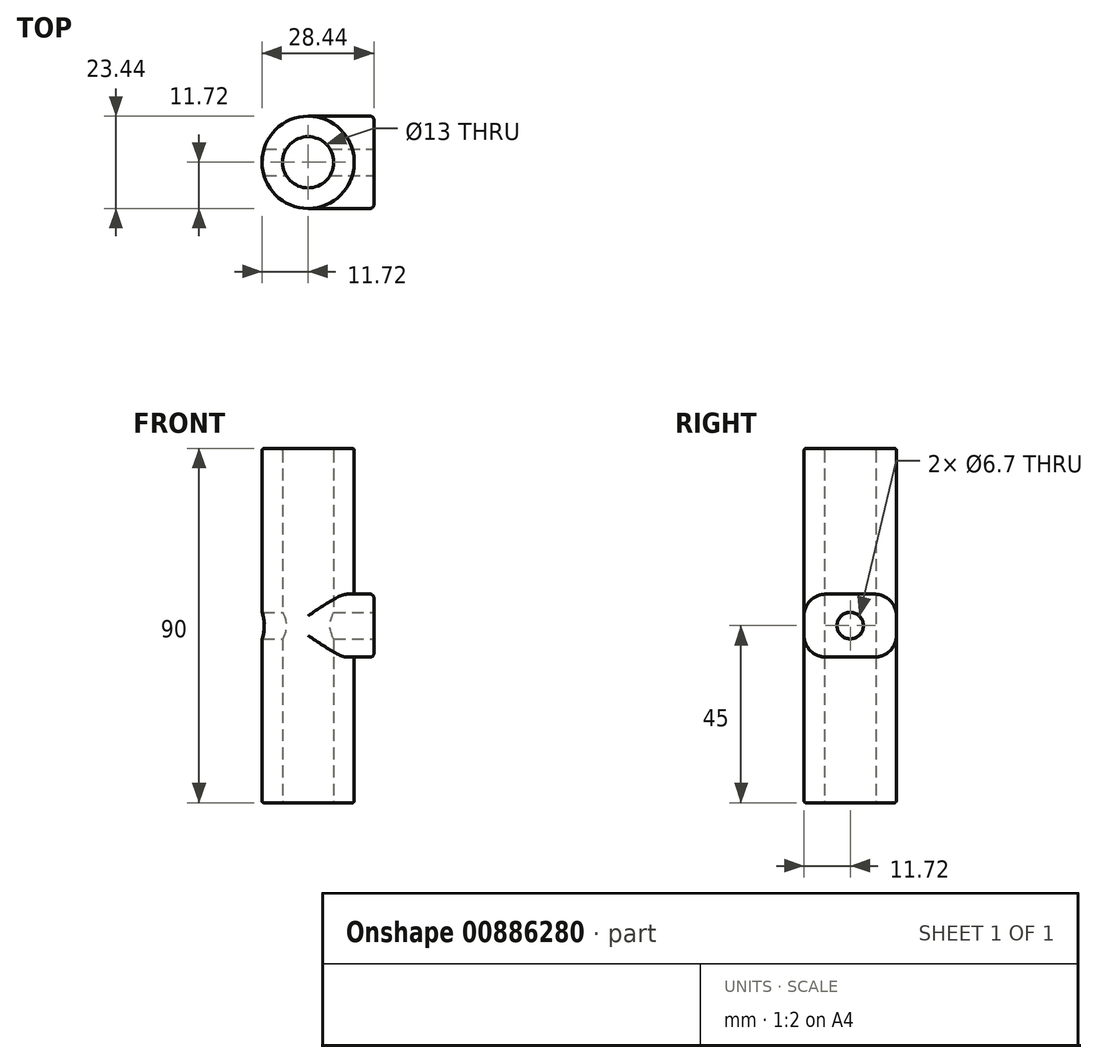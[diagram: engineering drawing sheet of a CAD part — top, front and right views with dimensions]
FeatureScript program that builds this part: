
annotation { "Feature Type Name" : "Feature", "Feature Type Description" : "" }
export const myFeature = defineFeature(function(context is Context, id is Id, definition is map)
    precondition{}
    {
        {
            var Q0;
            Q0=qCreatedBy(makeId("Top.planeOp"),FACE);
            var sketch = newSketch(context, id + "F0", { "sketchPlane" : qUnion([Q0])});
            skArc(sketch, "E0", {"start": v(0, 11.72) * mm, "mid": v(-11.72, 0) * mm, "end": v(0, -11.72) * mm});
            skLineSegment(sketch, "E1", {"start": v(0, 11.72) * mm, "end": v(16.72, 11.72) * mm});
            skLineSegment(sketch, "E2", {"start": v(16.72, 11.72) * mm, "end": v(16.72, -11.72) * mm});
            skLineSegment(sketch, "E3", {"start": v(16.72, -11.72) * mm, "end": v(0, -11.72) * mm});
            skCircle(sketch, "E4", {"center": v(0, 0) * mm, "radius": 6.5 * mm});
            skCircle(sketch, "E5", {"center": v(0, 0) * mm, "radius": 11.72 * mm});
            skSolve(sketch);
        }
        {
            var Q0;
            Q0=makeQuery(id+"F0.imprint","IMPRINT",FACE,{"disambiguationData":[TD([[makeQuery(id+"F0.imprint","IMPRINT",EDGE,{"derivedFrom":sQuery(id+"F0.wireOp",EDGE,"E4")}),-1.0]])]});
            extrude(context, id + "F1", {"entities" : qUnion([Q0]), "depth" : 45 * mm, "offsetDistance" : 25 * mm});
        }
        {
            var Q0;
            Q0=makeQuery(id+"F1.opExtrude","CAP_FACE",FACE,{"disambiguationData":[OSD([sQuery(id+"F0.wireOp",EDGE,"E4"),sQuery(id+"F0.wireOp",EDGE,"E5")])],"isStart":true});
            extrude(context, id + "F2", {"entities" : qUnion([Q0]), "operationType" : NewBodyOperationType.ADD, "depth" : 45 * mm, "offsetDistance" : 25 * mm});
        }
        {
            var Q0;
            {var subQ0=sQuery(id+"F0.wireOp",EDGE,"E1");Q0=makeQuery(id+"F0.imprint","IMPRINT",FACE,{"disambiguationData":[TD([[makeQuery(id+"F0.imprint","IMPRINT",EDGE,{"derivedFrom":subQ0}),-1.0]])]});}
            extrude(context, id + "F3", {"entities" : qUnion([Q0]), "operationType" : NewBodyOperationType.ADD, "depth" : 8 * mm, "offsetDistance" : 25 * mm, "hasSecondDirection" : true, "secondDirectionOppositeDirection" : true, "secondDirectionDepth" : 8 * mm});
        }
        {
            var Q0;
            Q0=makeQuery(id+"F3.opExtrude","CAP_EDGE",EDGE,{"disambiguationData":[OSD([sQuery(id+"F0.wireOp",EDGE,"E1")])],"isStart":false});
            var Q1;
            Q1=makeQuery(id+"F3.opExtrude","CAP_EDGE",EDGE,{"disambiguationData":[OSD([sQuery(id+"F0.wireOp",EDGE,"E1")])],"isStart":true});
            var Q2;
            Q2=makeQuery(id+"F3.opExtrude","CAP_EDGE",EDGE,{"disambiguationData":[OSD([sQuery(id+"F0.wireOp",EDGE,"E3")])],"isStart":true});
            var Q3;
            Q3=makeQuery(id+"F3.opExtrude","CAP_EDGE",EDGE,{"disambiguationData":[OSD([sQuery(id+"F0.wireOp",EDGE,"E3")])],"isStart":false});
            var Q4;
            Q4=makeQuery(id+"F3.opExtrude","CAP_EDGE",EDGE,{"disambiguationData":[OSD([sQuery(id+"F0.wireOp",EDGE,"E5")])],"isStart":false});
            var Q5;
            Q5=makeQuery(id+"F3.opExtrude","CAP_EDGE",EDGE,{"disambiguationData":[OSD([sQuery(id+"F0.wireOp",EDGE,"E5")])],"isStart":true});
            fillet(context, id + "F4", {"entities" : qUnion([Q0, Q1, Q2, Q3, Q4, Q5]), "radius" : 5.5 * mm, "tangentPropagation" : true, "allowEdgeOverflow" : false});
        }
        {
            var Q0;
            Q0=makeQuery(id+"F3.opExtrude","SWEPT_FACE",FACE,{"disambiguationData":[OSD([sQuery(id+"F0.wireOp",EDGE,"E2")])]});
            fillet(context, id + "F5", {"entities" : qUnion([Q0]), "radius" : 1 * mm, "tangentPropagation" : true, "allowEdgeOverflow" : false});
        }
        {
            var Q0;
            Q0=makeQuery(id+"F3.opExtrude","SWEPT_FACE",FACE,{"disambiguationData":[OSD([sQuery(id+"F0.wireOp",EDGE,"E2")])]});
            var sketch = newSketch(context, id + "F6", { "sketchPlane" : qUnion([Q0])});
            skCircle(sketch, "E6", {"center": v(0, 0) * mm, "radius": 3.35 * mm});
            skSolve(sketch);
        }
        {
            var Q0;
            Q0=makeQuery(id+"F6.imprint","IMPRINT",FACE,{"disambiguationData":[TD([[makeQuery(id+"F6.imprint","IMPRINT",EDGE,{"derivedFrom":sQuery(id+"F6.wireOp",EDGE,"E6")}),1.0]])]});
            extrude(context, id + "F7", {"entities" : qUnion([Q0]), "operationType" : NewBodyOperationType.REMOVE, "oppositeDirection" : true, "depth" : 59.87 * mm, "offsetDistance" : 25 * mm});
        }
        {
            var Q0;
            {var subQ0=sQuery(id+"F0.wireOp",EDGE,"E5");Q0=makeQuery(id+"F7.boolean.opBoolean","INTERSECT",EDGE,{"derivedFrom":[makeQuery(id+"F2.boolean.opBoolean","MERGE",FACE,{"derivedFrom":[makeQuery(id+"F1.opExtrude","SWEPT_FACE",FACE,{"disambiguationData":[OSD([subQ0])]}),makeQuery(id+"F2.opExtrude","SWEPT_FACE",FACE,{"disambiguationData":[OSD([subQ0])]})]}),makeQuery(id+"F7.opExtrude","SWEPT_FACE",FACE,{"disambiguationData":[OSD([sQuery(id+"F6.wireOp",EDGE,"E6")])]})]});}
            var Q1;
            Q1=makeQuery(id+"F7.boolean.opBoolean","COPY",EDGE,{"derivedFrom":makeQuery(id+"F7.opExtrude","CAP_EDGE",EDGE,{"disambiguationData":[OSD([sQuery(id+"F6.wireOp",EDGE,"E6")])],"isStart":true})});
            fillet(context, id + "F8", {"entities" : qUnion([Q0, Q1]), "radius" : 0.2 * mm, "tangentPropagation" : true, "allowEdgeOverflow" : false});
        }
        {
            var Q0;
            Q0=makeQuery(id+"F1.opExtrude","CAP_EDGE",EDGE,{"disambiguationData":[OSD([sQuery(id+"F0.wireOp",EDGE,"E4")])],"isStart":false});
            var Q1;
            Q1=makeQuery(id+"F2.opExtrude","CAP_EDGE",EDGE,{"disambiguationData":[OSD([sQuery(id+"F0.wireOp",EDGE,"E4")])],"isStart":false});
            fillet(context, id + "F9", {"entities" : qUnion([Q0, Q1]), "radius" : 0.5 * mm, "tangentPropagation" : true, "allowEdgeOverflow" : false});
        }
        {
            var Q0;
            Q0=makeQuery(id+"F2.opExtrude","CAP_EDGE",EDGE,{"disambiguationData":[OSD([sQuery(id+"F0.wireOp",EDGE,"E5")])],"isStart":false});
            var Q1;
            Q1=makeQuery(id+"F1.opExtrude","CAP_EDGE",EDGE,{"disambiguationData":[OSD([sQuery(id+"F0.wireOp",EDGE,"E5")])],"isStart":false});
            fillet(context, id + "F10", {"entities" : qUnion([Q0, Q1]), "radius" : 0.5 * mm, "tangentPropagation" : true, "allowEdgeOverflow" : false});
        }
    });
